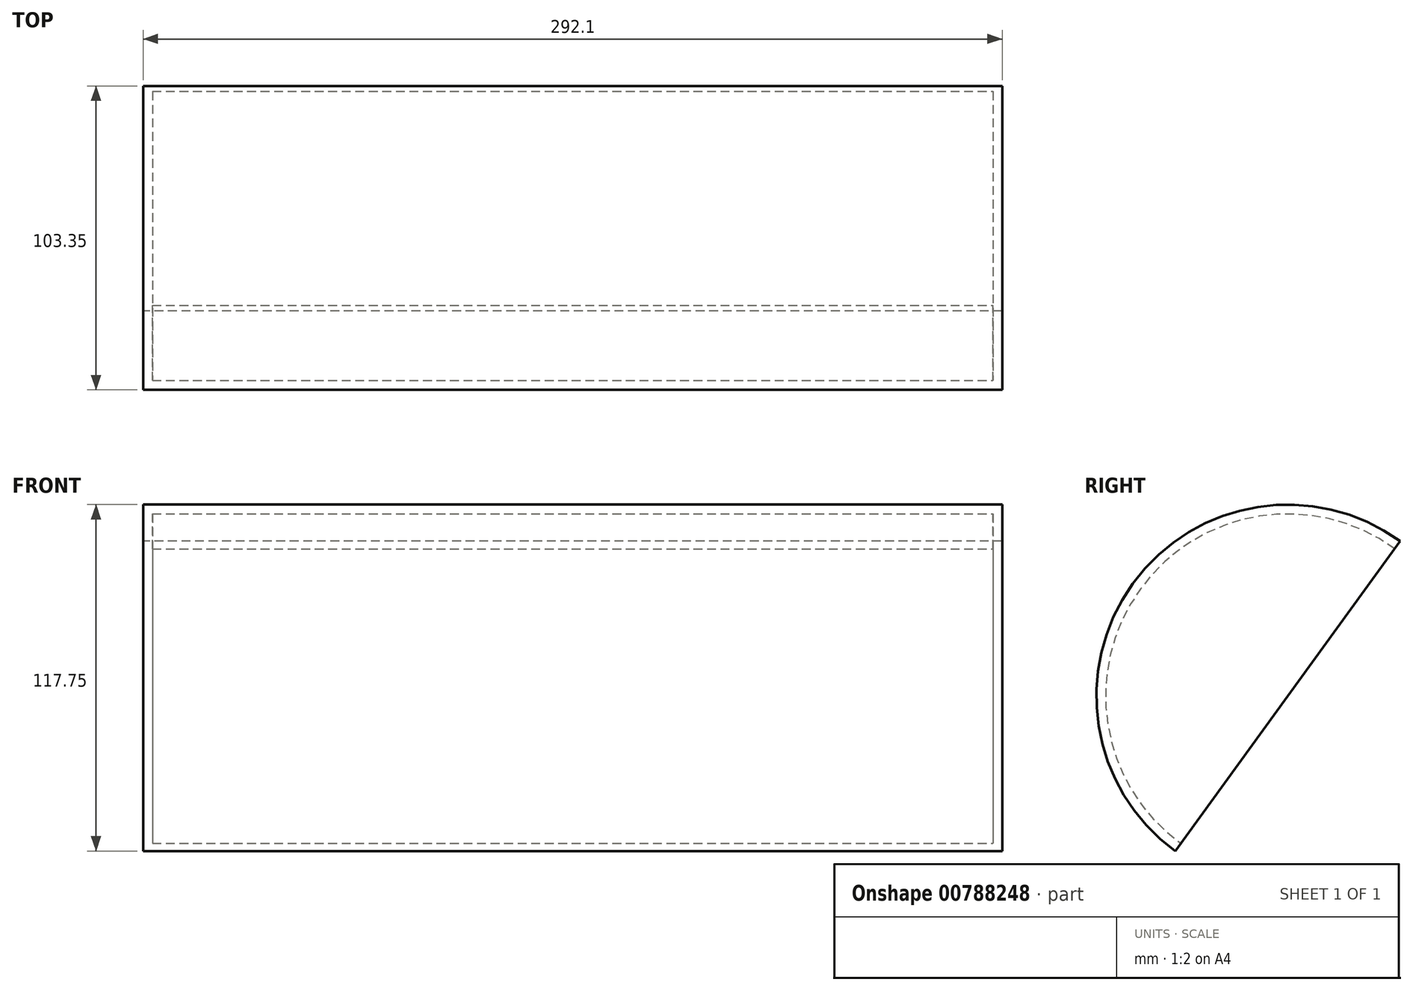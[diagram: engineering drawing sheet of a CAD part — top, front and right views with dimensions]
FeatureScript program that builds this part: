
annotation { "Feature Type Name" : "Feature", "Feature Type Description" : "" }
export const myFeature = defineFeature(function(context is Context, id is Id, definition is map)
    precondition{}
    {
        {
            var Q0;
            Q0=qCreatedBy(makeId("Right.planeOp"),FACE);
            var sketch = newSketch(context, id + "F0", { "sketchPlane" : qUnion([Q0])});
            skCircle(sketch, "E0", {"center": v(0, 0) * mm, "radius": 65.09 * mm});
            skLineSegment(sketch, "E1", {"start": v(-38.26, -52.66) * mm, "end": v(38.26, 52.66) * mm});
            skSolve(sketch);
        }
        {
            var Q0;
            {var subQ0=sQuery(id+"F0.wireOp",EDGE,"E1");Q0=makeQuery(id+"F0.imprint","IMPRINT",FACE,{"disambiguationData":[TD([[makeQuery(id+"F0.imprint","IMPRINT",EDGE,{"derivedFrom":subQ0}),1.0]])]});}
            extrude(context, id + "F1", {"entities" : qUnion([Q0]), "depth" : 292.1 * mm, "offsetDistance" : 25.4 * mm});
        }
        {
            var Q0;
            Q0=makeQuery(id+"F1.opExtrude","SWEPT_FACE",FACE,{"disambiguationData":[OSD([sQuery(id+"F0.wireOp",EDGE,"E1")])]});
            var sketch = newSketch(context, id + "F2", { "sketchPlane" : qUnion([Q0])});
            skLineSegment(sketch, "E2.0", {"start": v(-288.93, -61.91) * mm, "end": v(-3.17, -61.91) * mm});
            skLineSegment(sketch, "E2.1", {"start": v(-288.93, -61.91) * mm, "end": v(-288.93, 61.91) * mm});
            skLineSegment(sketch, "E2.2", {"start": v(-288.93, 61.91) * mm, "end": v(-3.17, 61.91) * mm});
            skLineSegment(sketch, "E2.3", {"start": v(-3.17, -61.91) * mm, "end": v(-3.17, 61.91) * mm});
            skLineSegment(sketch, "E3", {"start": v(-3.17, 0) * mm, "end": v(-288.93, 0) * mm});
            skSolve(sketch);
        }
        {
            var Q0;
            {var subQ0=sQuery(id+"F2.wireOp",EDGE,"E2.0");Q0=makeQuery(id+"F2.imprint","IMPRINT",FACE,{"disambiguationData":[TD([[makeQuery(id+"F2.imprint","IMPRINT",EDGE,{"derivedFrom":subQ0}),1.0]])]});}
            var Q1;
            Q1=sQuery(id+"F2.wireOp",EDGE,"E3");
            revolve(context, id + "F3", {"operationType" : NewBodyOperationType.REMOVE, "surfaceOperationType" : NewSurfaceOperationType.NEW, "entities" : qUnion([Q0]), "axis" : qUnion([Q1]), "revolveType" : RevolveType.FULL, "oppositeDirection" : true});
        }
    });
